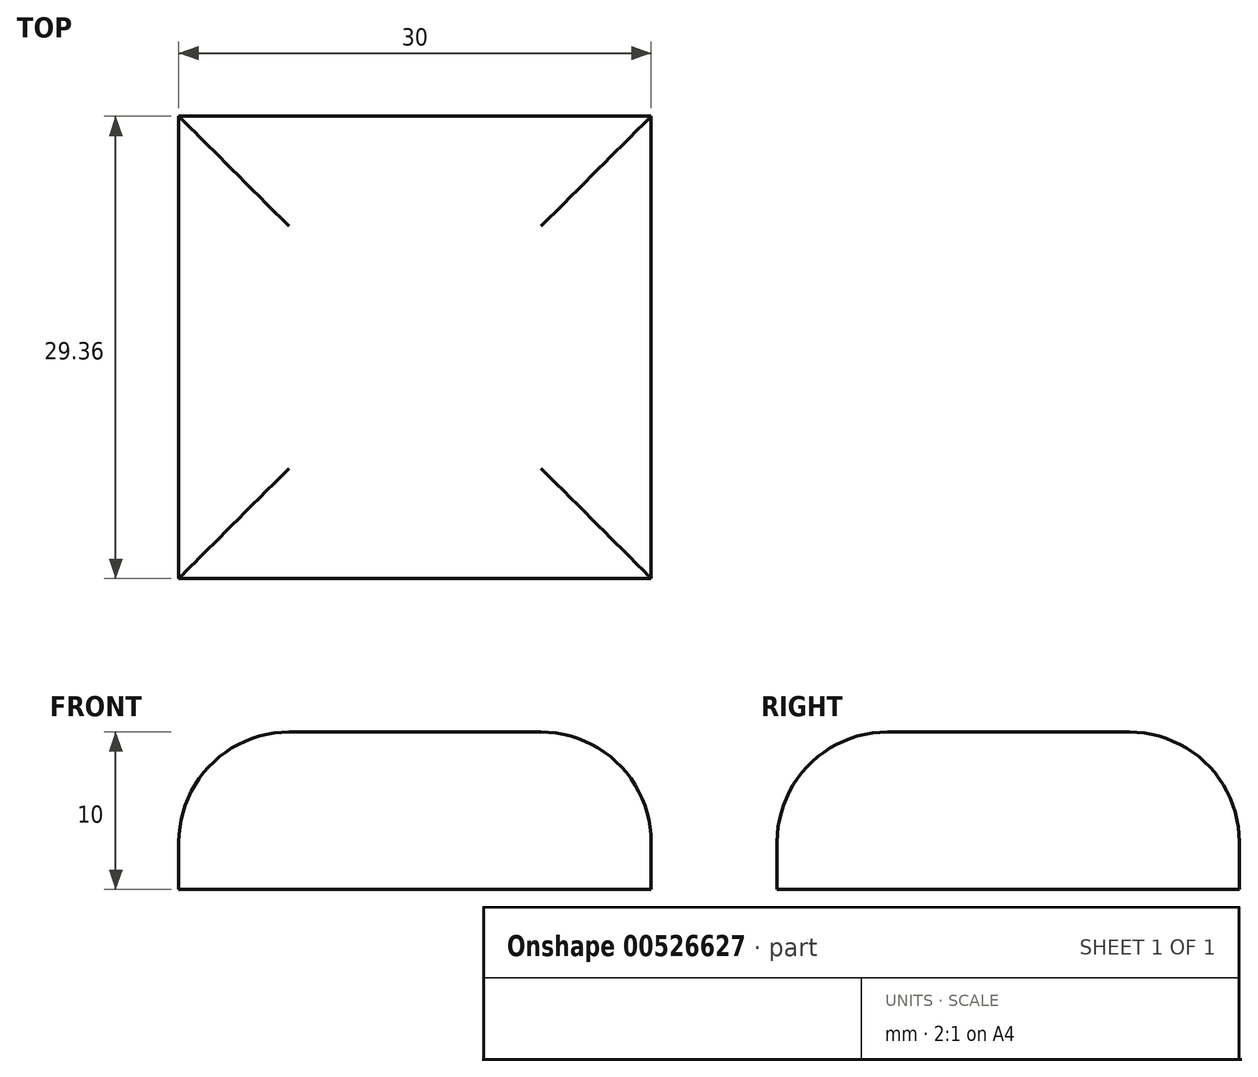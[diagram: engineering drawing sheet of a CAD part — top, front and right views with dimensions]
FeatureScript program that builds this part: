
annotation { "Feature Type Name" : "Feature", "Feature Type Description" : "" }
export const myFeature = defineFeature(function(context is Context, id is Id, definition is map)
    precondition{}
    {
        {
            var Q0;
            Q0=qCreatedBy(makeId("Top.planeOp"),FACE);
            var sketch = newSketch(context, id + "F0", { "sketchPlane" : qUnion([Q0])});
            skLineSegment(sketch, "E0.bottom", {"start": v(15, -14.68) * mm, "end": v(-15, -14.68) * mm});
            skLineSegment(sketch, "E0.top", {"start": v(15, 14.68) * mm, "end": v(-15, 14.68) * mm});
            skLineSegment(sketch, "E0.left", {"start": v(15, -14.68) * mm, "end": v(15, 14.68) * mm});
            skLineSegment(sketch, "E0.right", {"start": v(-15, -14.68) * mm, "end": v(-15, 14.68) * mm});
            skPoint(sketch, "E0.middle", {"position": v(0, 0) * mm});
            skSolve(sketch);
        }
        {
            var Q0;
            Q0 = qSketchRegion(id + "F0", true);
            extrude(context, id + "F1", {"entities" : qUnion([Q0]), "depth" : 10 * mm, "offsetDistance" : 25 * mm});
        }
        {
            var Q0;
            Q0=makeQuery(id+"F1.opExtrude","CAP_EDGE",EDGE,{"disambiguationData":[OSD([sQuery(id+"F0.wireOp",EDGE,"E0.left")])],"isStart":false});
            var Q1;
            Q1=makeQuery(id+"F1.opExtrude","CAP_EDGE",EDGE,{"disambiguationData":[OSD([sQuery(id+"F0.wireOp",EDGE,"E0.right")])],"isStart":false});
            var Q2;
            Q2=makeQuery(id+"F1.opExtrude","CAP_EDGE",EDGE,{"disambiguationData":[OSD([sQuery(id+"F0.wireOp",EDGE,"E0.bottom")])],"isStart":false});
            var Q3;
            Q3=makeQuery(id+"F1.opExtrude","CAP_EDGE",EDGE,{"disambiguationData":[OSD([sQuery(id+"F0.wireOp",EDGE,"E0.top")])],"isStart":false});
            fillet(context, id + "F2", {"entities" : qUnion([Q0, Q1, Q2, Q3]), "radius" : 7 * mm, "tangentPropagation" : true, "allowEdgeOverflow" : false});
        }
    });
